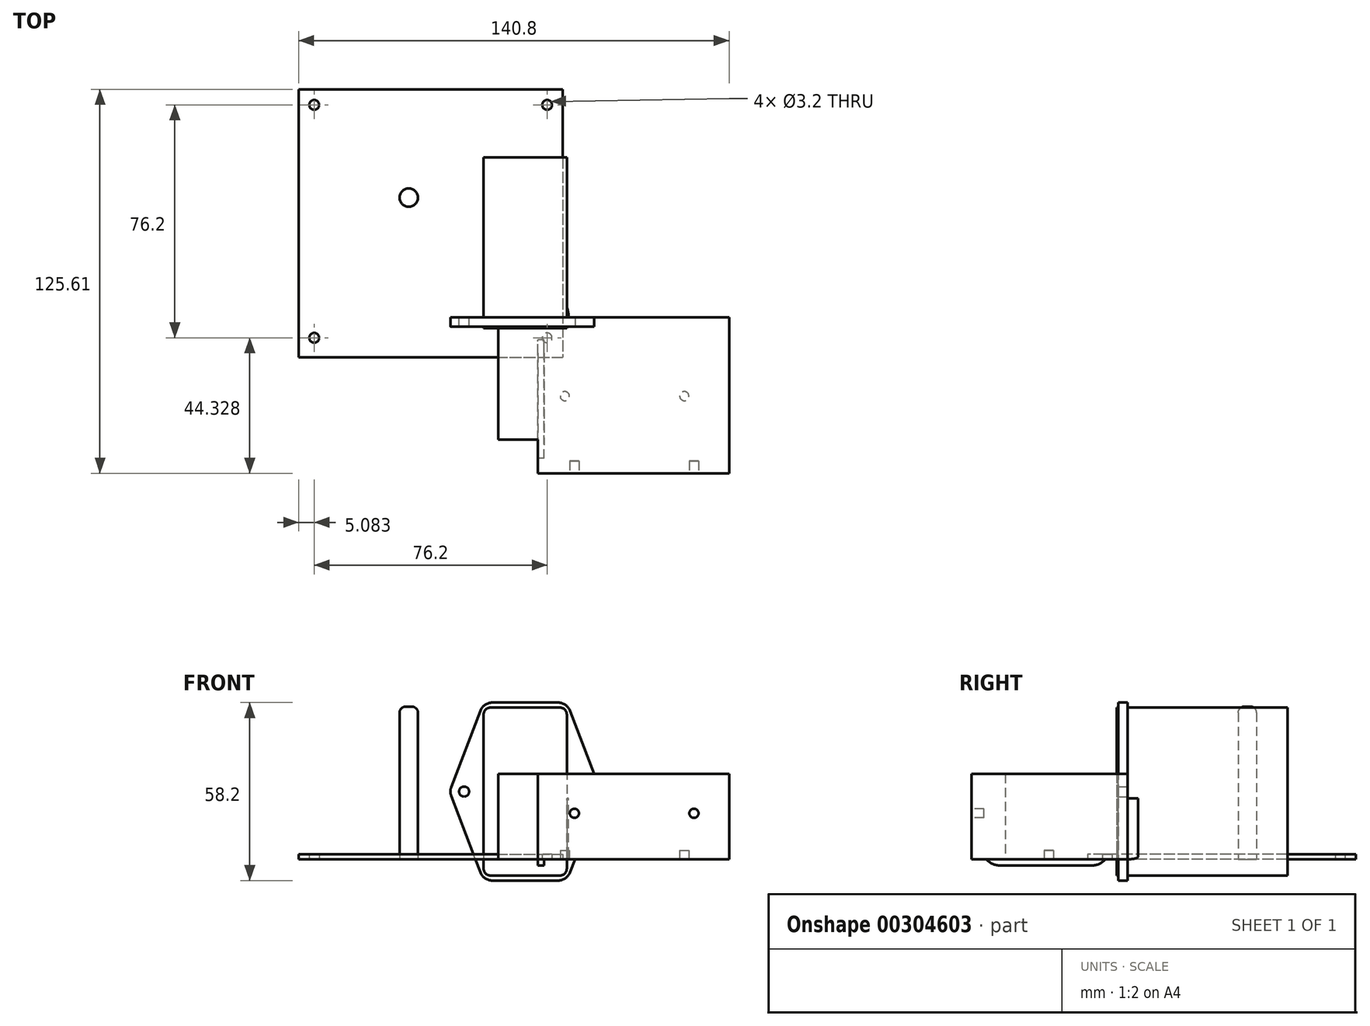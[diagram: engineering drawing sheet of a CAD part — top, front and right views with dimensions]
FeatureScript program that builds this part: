
annotation { "Feature Type Name" : "Feature", "Feature Type Description" : "" }
export const myFeature = defineFeature(function(context is Context, id is Id, definition is map)
    precondition{}
    {
        {
            var Q0;
            Q0=qCreatedBy(makeId("Front.planeOp"),FACE);
            var sketch = newSketch(context, id + "F0", { "sketchPlane" : qUnion([Q0])});
            skLineSegment(sketch, "E0", {"start": v(-14.94, 51.32) * mm, "end": v(6.55, 51.32) * mm});
            skLineSegment(sketch, "E1", {"start": v(10.48, 48.61) * mm, "end": v(19.98, 23.71) * mm});
            skLineSegment(sketch, "E2", {"start": v(19.98, 20.72) * mm, "end": v(10.48, -4.18) * mm});
            skLineSegment(sketch, "E3", {"start": v(6.55, -6.88) * mm, "end": v(-14.94, -6.88) * mm});
            skLineSegment(sketch, "E4", {"start": v(-18.86, -4.18) * mm, "end": v(-28.37, 20.72) * mm});
            skLineSegment(sketch, "E5", {"start": v(-28.37, 23.71) * mm, "end": v(-18.86, 48.61) * mm});
            skLineSegment(sketch, "E6", {"start": v(-45.26, 22.22) * mm, "end": v(30, 22.22) * mm, "construction": true});
            skLineSegment(sketch, "E7", {"start": v(-4.2, -24.04) * mm, "end": v(-4.2, 51.32) * mm, "construction": true});
            skPoint(sketch, "E7.startSnap0", {"position": v(-4.2, 51.32) * mm});
            skPoint(sketch, "E8.visualSharp", {"position": v(-17.83, 51.32) * mm});
            skPoint(sketch, "E9.visualSharp", {"position": v(9.44, 51.32) * mm});
            skPoint(sketch, "E10.visualSharp", {"position": v(20.56, 22.22) * mm});
            skPoint(sketch, "E11.visualSharp", {"position": v(9.44, -6.88) * mm});
            skPoint(sketch, "E12.visualSharp", {"position": v(-17.83, -6.88) * mm});
            skPoint(sketch, "E13.visualSharp", {"position": v(-28.94, 22.22) * mm});
            skCircle(sketch, "E14", {"center": v(-24.2, 22.22) * mm, "radius": 1.65 * mm});
            skCircle(sketch, "E15.MirrorC", {"center": v(15.8, 22.22) * mm, "radius": 1.65 * mm});
            skLineSegment(sketch, "E16.bottom", {"start": v(-15.6, 49.67) * mm, "end": v(7.2, 49.67) * mm});
            skLineSegment(sketch, "E16.top", {"start": v(-15.6, -5.23) * mm, "end": v(7.2, -5.23) * mm});
            skLineSegment(sketch, "E16.left", {"start": v(-17.8, 47.47) * mm, "end": v(-17.8, -3.03) * mm});
            skLineSegment(sketch, "E16.right", {"start": v(9.4, 47.47) * mm, "end": v(9.4, -3.03) * mm});
            skPoint(sketch, "E17.visualSharp", {"position": v(-17.8, -5.23) * mm});
            skArc(sketch, "E17.filletArc", {"start": v(-17.8, -3.03) * mm, "mid": v(-17.15, -4.6) * mm, "end": v(-15.6, -5.23) * mm});
            skPoint(sketch, "E18.visualSharp", {"position": v(-17.8, 49.67) * mm});
            skArc(sketch, "E18.filletArc", {"start": v(-15.6, 49.67) * mm, "mid": v(-17.15, 49.02) * mm, "end": v(-17.8, 47.47) * mm});
            skPoint(sketch, "E19.visualSharp", {"position": v(9.4, 49.67) * mm});
            skArc(sketch, "E19.filletArc", {"start": v(9.4, 47.47) * mm, "mid": v(8.76, 49.02) * mm, "end": v(7.2, 49.67) * mm});
            skPoint(sketch, "E20.visualSharp", {"position": v(9.4, -5.23) * mm});
            skArc(sketch, "E20.filletArc", {"start": v(7.2, -5.23) * mm, "mid": v(8.76, -4.6) * mm, "end": v(9.4, -3.03) * mm});
            skArc(sketch, "E21.filletArc", {"start": v(-14.94, 51.32) * mm, "mid": v(-17.32, 50.57) * mm, "end": v(-18.86, 48.61) * mm});
            skArc(sketch, "E22.filletArc", {"start": v(10.48, 48.61) * mm, "mid": v(8.93, 50.57) * mm, "end": v(6.55, 51.32) * mm});
            skArc(sketch, "E23.filletArc", {"start": v(19.98, 20.72) * mm, "mid": v(20.26, 22.22) * mm, "end": v(19.98, 23.71) * mm});
            skArc(sketch, "E24.filletArc", {"start": v(6.55, -6.88) * mm, "mid": v(8.93, -6.14) * mm, "end": v(10.48, -4.18) * mm});
            skArc(sketch, "E25.filletArc", {"start": v(-18.86, -4.18) * mm, "mid": v(-17.32, -6.14) * mm, "end": v(-14.94, -6.88) * mm});
            skArc(sketch, "E26.filletArc", {"start": v(-28.37, 23.71) * mm, "mid": v(-28.65, 22.22) * mm, "end": v(-28.37, 20.72) * mm});
            skPoint(sketch, "E27", {"position": v(-4.2, 49.67) * mm});
            skPoint(sketch, "E28", {"position": v(-4.2, -5.23) * mm});
            skPoint(sketch, "E29", {"position": v(-17.8, 22.22) * mm});
            skPoint(sketch, "E30", {"position": v(9.4, 22.22) * mm});
            skSolve(sketch);
        }
        {
            var Q0;
            Q0=makeQuery(id+"F0.imprint","IMPRINT",FACE,{"disambiguationData":[TD([[makeQuery(id+"F0.imprint","IMPRINT",EDGE,{"derivedFrom":sQuery(id+"F0.wireOp",EDGE,"E0")}),-1.0]])]});
            extrude(context, id + "F1", {"entities" : qUnion([Q0]), "depth" : 3 * mm});
        }
        {
            var Q0;
            Q0=qCreatedBy(makeId("Top.planeOp"),FACE);
            var sketch = newSketch(context, id + "F2", { "sketchPlane" : qUnion([Q0])});
            skLineSegment(sketch, "E31.bottom", {"start": v(0, 0) * mm, "end": v(62.5, 0) * mm});
            skLineSegment(sketch, "E31.top", {"start": v(0, -51) * mm, "end": v(62.5, -51) * mm});
            skLineSegment(sketch, "E31.left", {"start": v(0, 0) * mm, "end": v(0, -51) * mm});
            skLineSegment(sketch, "E31.right", {"start": v(62.5, 0) * mm, "end": v(62.5, -51) * mm});
            skLineSegment(sketch, "E32", {"start": v(0, -0.34) * mm, "end": v(-13, -0.34) * mm});
            skLineSegment(sketch, "E33", {"start": v(-13, -0.34) * mm, "end": v(-13, -40) * mm});
            skLineSegment(sketch, "E34", {"start": v(-13, -40) * mm, "end": v(0, -40) * mm});
            skLineSegment(sketch, "E35", {"start": v(0, -25.75) * mm, "end": v(62.5, -25.75) * mm, "construction": true});
            skLineSegment(sketch, "E36", {"start": v(47.85, -25.75) * mm, "end": v(47.85, -51) * mm, "construction": true});
            skLineSegment(sketch, "E37", {"start": v(8.75, -25.75) * mm, "end": v(8.75, -51) * mm, "construction": true});
            skCircle(sketch, "E38", {"center": v(8.75, -25.75) * mm, "radius": 1.5 * mm});
            skCircle(sketch, "E39", {"center": v(47.85, -25.75) * mm, "radius": 1.5 * mm});
            skSolve(sketch);
        }
        {
            var Q0;
            Q0 = qSketchRegion(id + "F2", true);
            var Q1;
            Q1=makeQuery(id+"F2.imprint","IMPRINT",FACE,{"disambiguationData":[TD([[makeQuery(id+"F2.imprint","IMPRINT",EDGE,{"derivedFrom":sQuery(id+"F2.wireOp",EDGE,"E38")}),1.0]])]});
            var Q2;
            Q2=makeQuery(id+"F2.imprint","IMPRINT",FACE,{"disambiguationData":[TD([[makeQuery(id+"F2.imprint","IMPRINT",EDGE,{"derivedFrom":sQuery(id+"F2.wireOp",EDGE,"E39")}),1.0]])]});
            extrude(context, id + "F3", {"entities" : qUnion([Q0, Q1, Q2]), "depth" : 28 * mm});
        }
        {
            var Q0;
            Q0=makeQuery(id+"F3.opExtrude","SWEPT_FACE",FACE,{"disambiguationData":[OSD([sQuery(id+"F2.wireOp",EDGE,"E31.top")])]});
            var sketch = newSketch(context, id + "F4", { "sketchPlane" : qUnion([Q0])});
            skLineSegment(sketch, "E40", {"start": v(0, 15.1) * mm, "end": v(62.5, 15.1) * mm, "construction": true});
            skLineSegment(sketch, "E41", {"start": v(51, 15.1) * mm, "end": v(51, 0) * mm, "construction": true});
            skLineSegment(sketch, "E42", {"start": v(11.9, 15.1) * mm, "end": v(11.9, 0) * mm, "construction": true});
            skCircle(sketch, "E43", {"center": v(11.9, 15.1) * mm, "radius": 1.5 * mm});
            skCircle(sketch, "E44", {"center": v(51, 15.1) * mm, "radius": 1.5 * mm});
            skSolve(sketch);
        }
        {
            var Q0;
            Q0=makeQuery(id+"F4.imprint","IMPRINT",FACE,{"disambiguationData":[TD([[makeQuery(id+"F4.imprint","IMPRINT",EDGE,{"derivedFrom":sQuery(id+"F4.wireOp",EDGE,"E43")}),1.0]])]});
            var Q1;
            Q1=makeQuery(id+"F4.imprint","IMPRINT",FACE,{"disambiguationData":[TD([[makeQuery(id+"F4.imprint","IMPRINT",EDGE,{"derivedFrom":sQuery(id+"F4.wireOp",EDGE,"E44")}),1.0]])]});
            extrude(context, id + "F5", {"entities" : qUnion([Q0, Q1]), "operationType" : NewBodyOperationType.REMOVE, "oppositeDirection" : true, "depth" : 4 * mm});
        }
        {
            var Q0;
            Q0=makeQuery(id+"F3.opExtrude","CAP_FACE",FACE,{"disambiguationData":[OSD([sQuery(id+"F2.wireOp",EDGE,"E31.bottom"),sQuery(id+"F2.wireOp",EDGE,"E31.top"),sQuery(id+"F2.wireOp",EDGE,"E31.left"),sQuery(id+"F2.wireOp",EDGE,"E31.right"),sQuery(id+"F2.wireOp",EDGE,"E32"),sQuery(id+"F2.wireOp",EDGE,"E33"),sQuery(id+"F2.wireOp",EDGE,"E34")])],"isStart":true});
            var sketch = newSketch(context, id + "F6", { "sketchPlane" : qUnion([Q0])});
            skCircle(sketch, "E45.0", {"center": v(8.75, 25.75) * mm, "radius": 1.5 * mm});
            skCircle(sketch, "E46.0", {"center": v(47.85, 25.75) * mm, "radius": 1.5 * mm});
            skSolve(sketch);
        }
        {
            var Q0;
            Q0 = qSketchRegion(id + "F6", true);
            extrude(context, id + "F7", {"entities" : qUnion([Q0]), "operationType" : NewBodyOperationType.REMOVE, "oppositeDirection" : true, "depth" : 3 * mm});
        }
        {
            var Q0;
            Q0=qCreatedBy(makeId("Front.planeOp"),FACE);
            var sketch = newSketch(context, id + "F8", { "sketchPlane" : qUnion([Q0])});
            skLineSegment(sketch, "E47", {"start": v(0, 0) * mm, "end": v(0, 33.88) * mm, "construction": true});
            skLineSegment(sketch, "E48", {"start": v(0, 0) * mm, "end": v(10, 0) * mm});
            skLineSegment(sketch, "E49", {"start": v(10, 0) * mm, "end": v(10, 20) * mm});
            skLineSegment(sketch, "E50", {"start": v(10, 20) * mm, "end": v(3, 20) * mm});
            skLineSegment(sketch, "E51", {"start": v(3, 20) * mm, "end": v(3, 38) * mm});
            skLineSegment(sketch, "E52", {"start": v(3, 38) * mm, "end": v(0, 38) * mm});
            skLineSegment(sketch, "E53", {"start": v(0, 38) * mm, "end": v(0, 0) * mm});
            skSolve(sketch);
        }
        {
            var Q0;
            Q0=makeQuery(id+"F8.imprint","IMPRINT",FACE,{"disambiguationData":[TD([[makeQuery(id+"F8.imprint","IMPRINT",EDGE,{"derivedFrom":sQuery(id+"F8.wireOp",EDGE,"E48")}),1.0]])]});
            var Q1;
            Q1=sQuery(id+"F8.wireOp",EDGE,"E53");
            revolve(context, id + "F9", {"entities" : qUnion([Q0]), "axis" : qUnion([Q1]), "revolveType" : RevolveType.FULL});
        }
        {
            var Q0;
            Q0=makeQuery(id+"F9.opRevolve","SWEPT_EDGE",EDGE,{"disambiguationData":[OSD([sQuery(id+"F8.wireOp",EDGE,"E48"),sQuery(id+"F8.wireOp",EDGE,"E49")])]});
            fillet(context, id + "F10", {"entities" : qUnion([Q0]), "radius" : 1 * mm, "tangentPropagation" : true, "allowEdgeOverflow" : false});
        }
        {
            var Q0;
            Q0=makeQuery(id+"F0.imprint","IMPRINT",FACE,{"disambiguationData":[TD([[makeQuery(id+"F0.imprint","IMPRINT",EDGE,{"derivedFrom":sQuery(id+"F0.wireOp",EDGE,"E16.bottom")}),-1.0]])]});
            extrude(context, id + "F11", {"entities" : qUnion([Q0]), "operationType" : NewBodyOperationType.ADD, "oppositeDirection" : true, "depth" : 52.3 * mm, "hasSecondDirection" : true, "secondDirectionOppositeDirection" : false, "secondDirectionDepth" : 3.5 * mm});
        }
        {
            var Q0;
            Q0=qCreatedBy(makeId("Top.planeOp"),FACE);
            var sketch = newSketch(context, id + "F12", { "sketchPlane" : qUnion([Q0])});
            skCircle(sketch, "E54", {"center": v(-42.29, 39.2) * mm, "radius": 3 * mm});
            skSolve(sketch);
        }
        {
            var Q0;
            Q0=makeQuery(id+"F12.imprint","IMPRINT",FACE,{"disambiguationData":[TD([[makeQuery(id+"F12.imprint","IMPRINT",EDGE,{"derivedFrom":sQuery(id+"F12.wireOp",EDGE,"E54")}),1.0]])]});
            extrude(context, id + "F13", {"entities" : qUnion([Q0]), "depth" : 50 * mm});
        }
        {
            var Q0;
            Q0=makeQuery(id+"F13.opExtrude","CAP_EDGE",EDGE,{"disambiguationData":[OSD([sQuery(id+"F12.wireOp",EDGE,"E54")])],"isStart":false});
            fillet(context, id + "F14", {"entities" : qUnion([Q0]), "radius" : 2 * mm, "tangentPropagation" : true, "allowEdgeOverflow" : false});
        }
        {
            var Q0;
            Q0=qCreatedBy(makeId("Top.planeOp"),FACE);
            var sketch = newSketch(context, id + "F15", { "sketchPlane" : qUnion([Q0])});
            skLineSegment(sketch, "E55.bottom", {"start": v(-78.3, 74.6) * mm, "end": v(8.06, 74.6) * mm});
            skLineSegment(sketch, "E55.top", {"start": v(-78.3, -13.02) * mm, "end": v(8.06, -13.02) * mm});
            skLineSegment(sketch, "E55.left", {"start": v(-78.3, 74.6) * mm, "end": v(-78.3, -13.02) * mm});
            skLineSegment(sketch, "E55.right", {"start": v(8.06, 74.6) * mm, "end": v(8.06, -13.02) * mm});
            skCircle(sketch, "E56", {"center": v(-73.22, -6.67) * mm, "radius": 1.6 * mm});
            skCircle(sketch, "E57", {"center": v(-73.22, 69.53) * mm, "radius": 1.6 * mm});
            skCircle(sketch, "E58", {"center": v(2.98, 69.53) * mm, "radius": 1.6 * mm});
            skCircle(sketch, "E59", {"center": v(2.98, -6.67) * mm, "radius": 1.6 * mm});
            skSolve(sketch);
        }
        {
            var Q0;
            Q0=makeQuery(id+"F15.imprint","IMPRINT",FACE,{"disambiguationData":[TD([[makeQuery(id+"F15.imprint","IMPRINT",EDGE,{"derivedFrom":sQuery(id+"F15.wireOp",EDGE,"E55.bottom")}),-1.0]])]});
            extrude(context, id + "F16", {"entities" : qUnion([Q0]), "depth" : 1.7 * mm});
        }
        {
            var Q0;
            Q0=qCreatedBy(makeId("Right.planeOp"),FACE);
            var sketch = newSketch(context, id + "F17", { "sketchPlane" : qUnion([Q0])});
            skCircle(sketch, "E60", {"center": v(-18.2, 5.55) * mm, "radius": 3.1 * mm});
            skLineSegment(sketch, "E61", {"start": v(-56.1, 5.55) * mm, "end": v(-4.37, 5.55) * mm, "construction": true});
            skLineSegment(sketch, "E62", {"start": v(-18.2, 14.48) * mm, "end": v(-18.2, -3) * mm, "construction": true});
            skCircle(sketch, "E63", {"center": v(-18.2, 5.55) * mm, "radius": 5.5 * mm});
            skCircle(sketch, "E64", {"center": v(-18.2, 5.55) * mm, "radius": 4.5 * mm});
            skLineSegment(sketch, "E65", {"start": v(-26.7, 14.83) * mm, "end": v(-26.7, -3.73) * mm, "construction": true});
            skCircle(sketch, "E66.MirrorC", {"center": v(-35.2, 5.55) * mm, "radius": 3.1 * mm});
            skCircle(sketch, "E67.MirrorC", {"center": v(-35.2, 5.55) * mm, "radius": 4.5 * mm});
            skCircle(sketch, "E68.MirrorC", {"center": v(-35.2, 5.55) * mm, "radius": 5.5 * mm});
            skLineSegment(sketch, "E69.bottom", {"start": v(-11.7, 13.05) * mm, "end": v(-41.7, 13.05) * mm});
            skLineSegment(sketch, "E69.top", {"start": v(-11.7, -1.95) * mm, "end": v(-41.7, -1.95) * mm});
            skLineSegment(sketch, "E69.left", {"start": v(-5.7, 7.05) * mm, "end": v(-5.7, 4.05) * mm});
            skLineSegment(sketch, "E69.right", {"start": v(-47.7, 7.05) * mm, "end": v(-47.7, 4.05) * mm});
            skPoint(sketch, "E69.middle", {"position": v(-26.7, 5.55) * mm});
            skCircle(sketch, "E70", {"center": v(-26.7, 5.55) * mm, "radius": 1.6 * mm});
            skPoint(sketch, "E71.visualSharp", {"position": v(-47.7, 13.05) * mm});
            skArc(sketch, "E71.filletArc", {"start": v(-41.7, 13.05) * mm, "mid": v(-45.95, 11.3) * mm, "end": v(-47.7, 7.05) * mm});
            skPoint(sketch, "E72.visualSharp", {"position": v(-5.7, 13.05) * mm});
            skArc(sketch, "E72.filletArc", {"start": v(-5.7, 7.05) * mm, "mid": v(-7.46, 11.3) * mm, "end": v(-11.7, 13.05) * mm});
            skPoint(sketch, "E73.visualSharp", {"position": v(-5.7, -1.95) * mm});
            skArc(sketch, "E73.filletArc", {"start": v(-11.7, -1.95) * mm, "mid": v(-7.46, -0.2) * mm, "end": v(-5.7, 4.05) * mm});
            skPoint(sketch, "E74.visualSharp", {"position": v(-47.7, -1.95) * mm});
            skArc(sketch, "E74.filletArc", {"start": v(-47.7, 4.05) * mm, "mid": v(-45.95, -0.2) * mm, "end": v(-41.7, -1.95) * mm});
            skCircle(sketch, "E75", {"center": v(-26.7, 5.55) * mm, "radius": 3 * mm, "construction": true});
            skCircle(sketch, "E76", {"center": v(-43.7, 5.55) * mm, "radius": 1.6 * mm});
            skCircle(sketch, "E77", {"center": v(-43.7, 5.55) * mm, "radius": 3 * mm, "construction": true});
            skCircle(sketch, "E78.MirrorC", {"center": v(-9.7, 5.55) * mm, "radius": 1.6 * mm});
            skSolve(sketch);
        }
        {
            var Q0;
            Q0=makeQuery(id+"F17.imprint","IMPRINT",FACE,{"disambiguationData":[TD([[makeQuery(id+"F17.imprint","IMPRINT",EDGE,{"derivedFrom":sQuery(id+"F17.wireOp",EDGE,"E63")}),-1.0]])]});
            extrude(context, id + "F18", {"entities" : qUnion([Q0]), "depth" : 2 * mm});
        }
        {
            var Q0;
            Q0=makeQuery(id+"F17.imprint","IMPRINT",FACE,{"disambiguationData":[TD([[makeQuery(id+"F17.imprint","IMPRINT",EDGE,{"derivedFrom":sQuery(id+"F17.wireOp",EDGE,"E67.MirrorC")}),1.0]])]});
            var Q1;
            Q1=makeQuery(id+"F17.imprint","IMPRINT",FACE,{"disambiguationData":[TD([[makeQuery(id+"F17.imprint","IMPRINT",EDGE,{"derivedFrom":sQuery(id+"F17.wireOp",EDGE,"E63")}),1.0]])]});
            extrude(context, id + "F19", {"entities" : qUnion([Q0, Q1]), "operationType" : NewBodyOperationType.ADD, "depth" : 3 * mm});
        }
        {
            var Q0;
            Q0=makeQuery(id+"F17.imprint","IMPRINT",FACE,{"disambiguationData":[TD([[makeQuery(id+"F17.imprint","IMPRINT",EDGE,{"derivedFrom":sQuery(id+"F17.wireOp",EDGE,"E66.MirrorC")}),1.0]])]});
            var Q1;
            Q1=makeQuery(id+"F17.imprint","IMPRINT",FACE,{"disambiguationData":[TD([[makeQuery(id+"F17.imprint","IMPRINT",EDGE,{"derivedFrom":sQuery(id+"F17.wireOp",EDGE,"E60")}),-1.0]])]});
            extrude(context, id + "F20", {"entities" : qUnion([Q0, Q1]), "operationType" : NewBodyOperationType.ADD, "depth" : 3 * mm, "hasSecondDirection" : true, "secondDirectionOppositeDirection" : false, "secondDirectionDepth" : 1 * mm});
        }
    });
